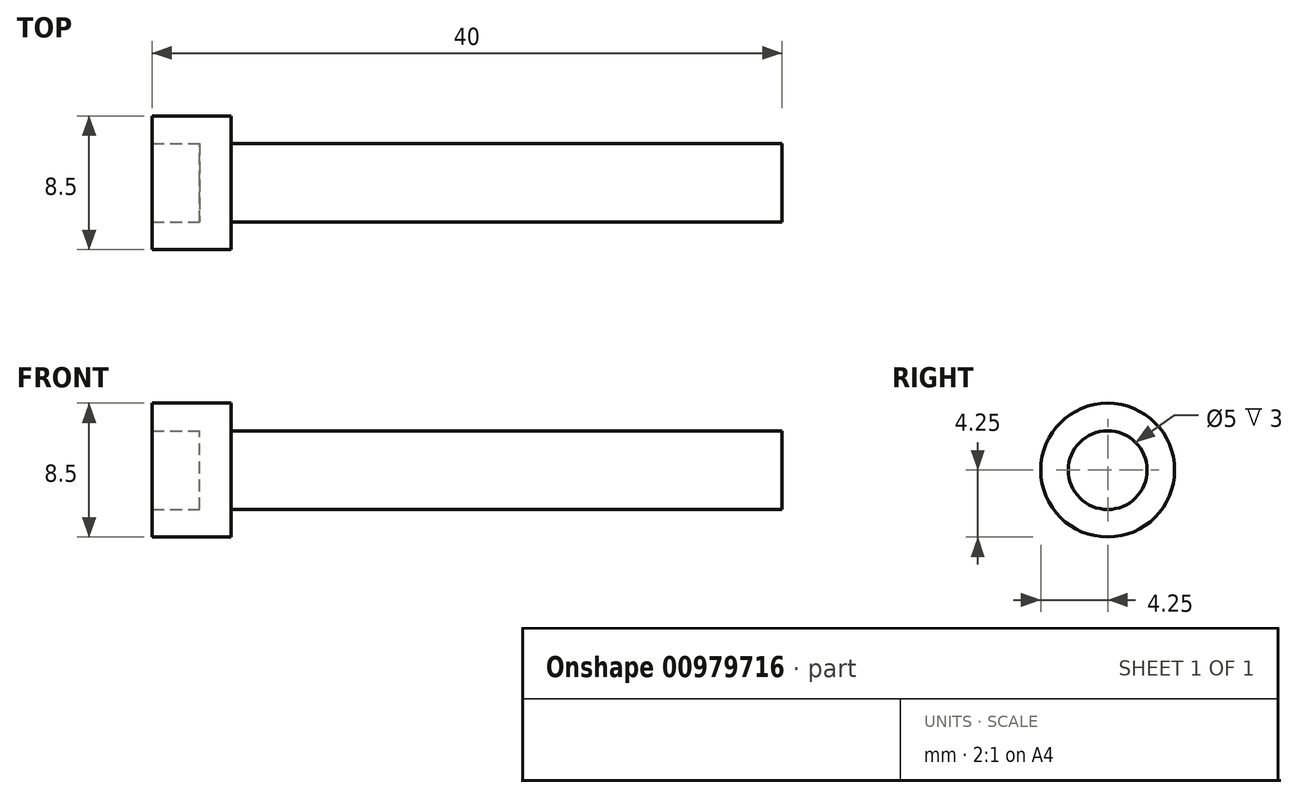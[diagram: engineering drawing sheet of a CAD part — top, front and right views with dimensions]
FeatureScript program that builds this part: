
annotation { "Feature Type Name" : "Feature", "Feature Type Description" : "" }
export const myFeature = defineFeature(function(context is Context, id is Id, definition is map)
    precondition{}
    {
        {
            var Q0;
            Q0=qCreatedBy(makeId("Front.planeOp"),FACE);
            var sketch = newSketch(context, id + "F0", { "sketchPlane" : qUnion([Q0])});
            skLineSegment(sketch, "E0.bottom", {"start": v(0, 0) * mm, "end": v(35, 0) * mm});
            skLineSegment(sketch, "E0.top", {"start": v(0, 2.5) * mm, "end": v(35, 2.5) * mm});
            skLineSegment(sketch, "E0.right", {"start": v(35, 0) * mm, "end": v(35, 2.5) * mm});
            skLineSegment(sketch, "E1.bottom", {"start": v(0, 0) * mm, "end": v(-5, 0) * mm});
            skLineSegment(sketch, "E1.top", {"start": v(0, 4.25) * mm, "end": v(-5, 4.25) * mm});
            skLineSegment(sketch, "E1.right", {"start": v(-5, 2.5) * mm, "end": v(-5, 4.25) * mm});
            skLineSegment(sketch, "E2", {"start": v(0, 4.25) * mm, "end": v(0, 2.5) * mm});
            skLineSegment(sketch, "E3", {"start": v(0, 0) * mm, "end": v(-2, 0) * mm, "construction": true});
            skLineSegment(sketch, "E4.bottom", {"start": v(-5, 0) * mm, "end": v(-2, 0) * mm});
            skLineSegment(sketch, "E4.top", {"start": v(-5, 2.5) * mm, "end": v(-2, 2.5) * mm});
            skLineSegment(sketch, "E4.right", {"start": v(-2, 0) * mm, "end": v(-2, 2.5) * mm});
            skLineSegment(sketch, "E5.trimOffspring", {"start": v(-5, 0) * mm, "end": v(-13.97, 0) * mm, "construction": true});
            skSolve(sketch);
        }
        {
            var Q0;
            Q0 = qSketchRegion(id + "F0", true);
            var Q1;
            Q1=sQuery(id+"F0.wireOp",EDGE,"E3");
            revolve(context, id + "F1", {"surfaceOperationType" : NewSurfaceOperationType.NEW, "entities" : qUnion([Q0]), "axis" : qUnion([Q1]), "revolveType" : RevolveType.FULL});
        }
    });
